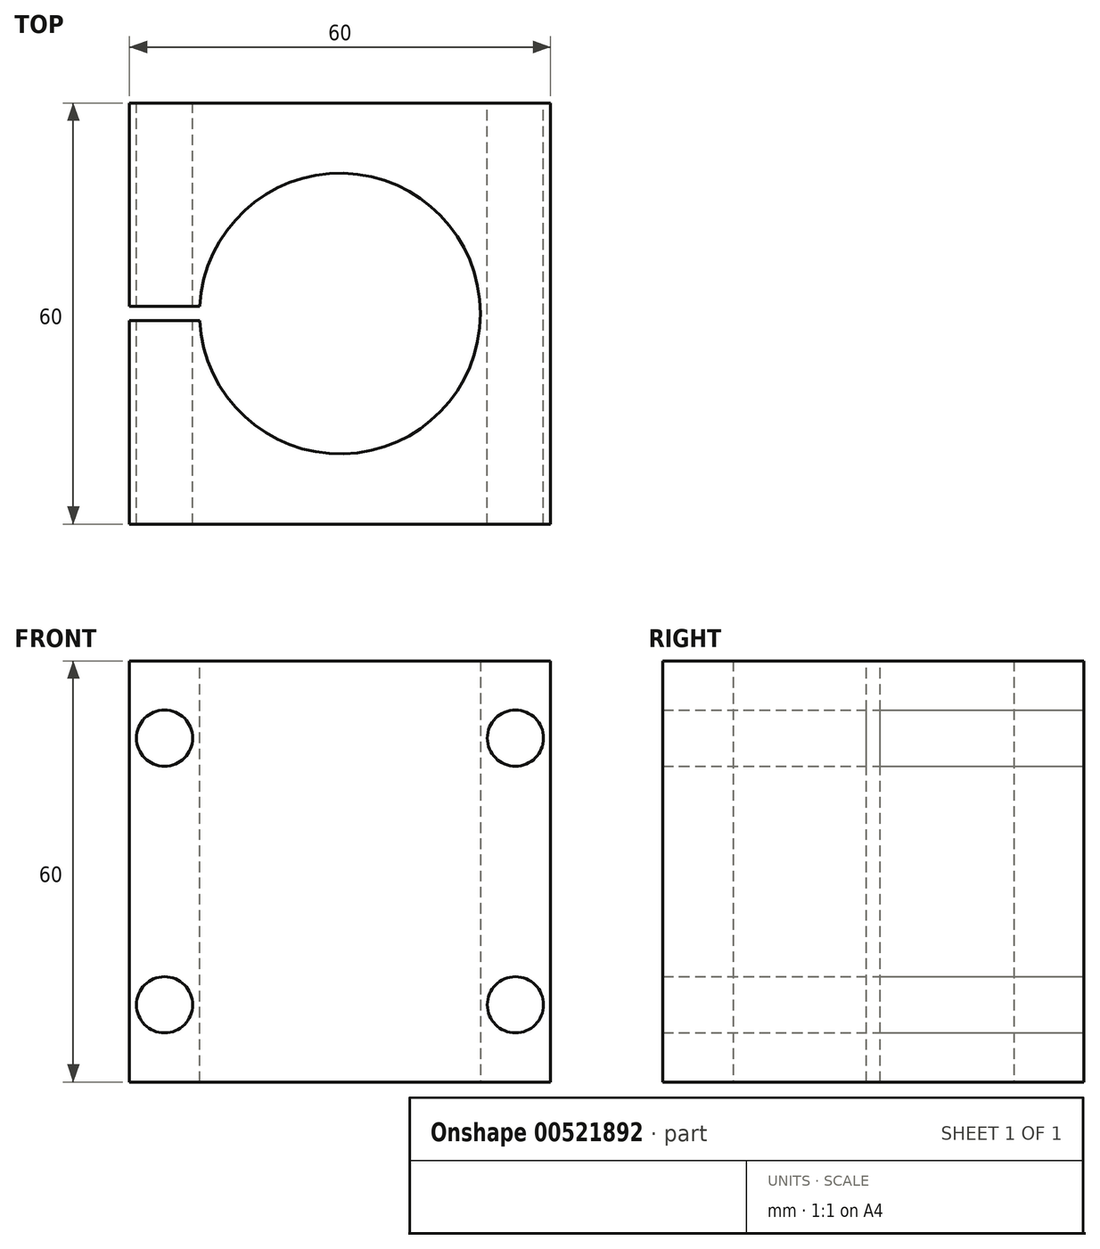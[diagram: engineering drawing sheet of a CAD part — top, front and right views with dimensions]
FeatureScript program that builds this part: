
annotation { "Feature Type Name" : "Feature", "Feature Type Description" : "" }
export const myFeature = defineFeature(function(context is Context, id is Id, definition is map)
    precondition{}
    {
        {
            var Q0;
            Q0=qCreatedBy(makeId("Top.planeOp"),FACE);
            var sketch = newSketch(context, id + "F0", { "sketchPlane" : qUnion([Q0])});
            skLineSegment(sketch, "E0.bottom", {"start": v(-30, 30) * mm, "end": v(30, 30) * mm});
            skLineSegment(sketch, "E0.top", {"start": v(-30, -30) * mm, "end": v(30, -30) * mm});
            skLineSegment(sketch, "E0.left", {"start": v(-30, 30) * mm, "end": v(-30, -30) * mm});
            skLineSegment(sketch, "E0.right", {"start": v(30, 30) * mm, "end": v(30, -30) * mm});
            skCircle(sketch, "E1", {"center": v(0, 0) * mm, "radius": 20 * mm});
            skSolve(sketch);
        }
        {
            var Q0;
            Q0 = qSketchRegion(id + "F0", true);
            extrude(context, id + "F1", {"entities" : qUnion([Q0]), "depth" : 60 * mm, "offsetDistance" : 25 * mm});
        }
        {
            var Q0;
            Q0=makeQuery(id+"F1.opExtrude","CAP_FACE",FACE,{"disambiguationData":[OSD([sQuery(id+"F0.wireOp",EDGE,"E0.bottom"),sQuery(id+"F0.wireOp",EDGE,"E0.top"),sQuery(id+"F0.wireOp",EDGE,"E0.left"),sQuery(id+"F0.wireOp",EDGE,"E0.right"),sQuery(id+"F0.wireOp",EDGE,"E1")])],"isStart":false});
            var sketch = newSketch(context, id + "F2", { "sketchPlane" : qUnion([Q0])});
            skLineSegment(sketch, "E2.bottom", {"start": v(-30, 1) * mm, "end": v(-19.97, 1) * mm});
            skLineSegment(sketch, "E2.top", {"start": v(-30, -1) * mm, "end": v(-19.97, -1) * mm});
            skLineSegment(sketch, "E2.left", {"start": v(-30, 1) * mm, "end": v(-30, -1) * mm});
            skLineSegment(sketch, "E2.right", {"start": v(-19.97, 1) * mm, "end": v(-19.97, -1) * mm});
            skSolve(sketch);
        }
        {
            var Q0;
            Q0 = qSketchRegion(id + "F2", true);
            extrude(context, id + "F3", {"entities" : qUnion([Q0]), "operationType" : NewBodyOperationType.REMOVE, "endBound" : BoundingType.THROUGH_ALL, "oppositeDirection" : true, "depth" : 25 * mm, "offsetDistance" : 25 * mm});
        }
        {
            var Q0;
            Q0=makeQuery(id+"F1.opExtrude","SWEPT_FACE",FACE,{"disambiguationData":[OSD([sQuery(id+"F0.wireOp",EDGE,"E0.bottom")])]});
            var sketch = newSketch(context, id + "F4", { "sketchPlane" : qUnion([Q0])});
            skLineSegment(sketch, "E3", {"start": v(30, 30) * mm, "end": v(-30, 30) * mm, "construction": true});
            skLineSegment(sketch, "E4", {"start": v(25, 0) * mm, "end": v(25, 60) * mm, "construction": true});
            skLineSegment(sketch, "E5", {"start": v(-25, 0) * mm, "end": v(-25, 60) * mm, "construction": true});
            skCircle(sketch, "E6", {"center": v(25, 11) * mm, "radius": 4 * mm});
            skCircle(sketch, "E7", {"center": v(25, 49) * mm, "radius": 4 * mm});
            skCircle(sketch, "E8", {"center": v(-25, 49) * mm, "radius": 4 * mm});
            skCircle(sketch, "E9", {"center": v(-25, 11) * mm, "radius": 4 * mm});
            skLineSegment(sketch, "E10", {"start": v(25, 11) * mm, "end": v(-25, 11) * mm, "construction": true});
            skLineSegment(sketch, "E11", {"start": v(-25, 49) * mm, "end": v(25, 49) * mm, "construction": true});
            skSolve(sketch);
        }
        {
            var Q0;
            Q0 = qSketchRegion(id + "F4", true);
            extrude(context, id + "F5", {"entities" : qUnion([Q0]), "operationType" : NewBodyOperationType.REMOVE, "oppositeDirection" : true, "depth" : 60 * mm, "offsetDistance" : 25 * mm});
        }
    });
